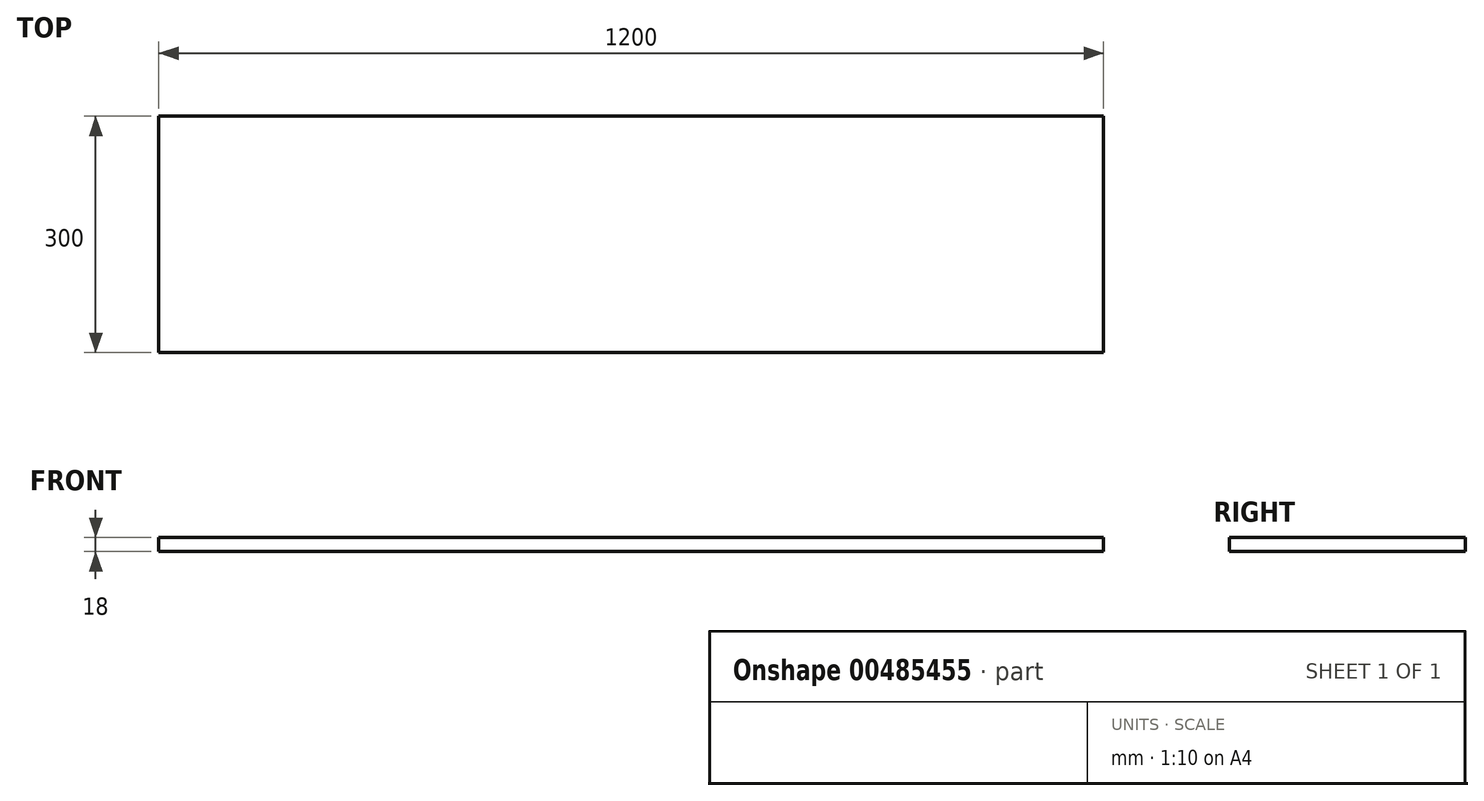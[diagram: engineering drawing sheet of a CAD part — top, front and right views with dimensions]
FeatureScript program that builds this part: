
annotation { "Feature Type Name" : "Feature", "Feature Type Description" : "" }
export const myFeature = defineFeature(function(context is Context, id is Id, definition is map)
    precondition{}
    {
        {
            var Q0;
            Q0=qCreatedBy(makeId("Top.planeOp"),FACE);
            var sketch = newSketch(context, id + "F0", { "sketchPlane" : qUnion([Q0])});
            skLineSegment(sketch, "E0.bottom", {"start": v(600, 150) * mm, "end": v(-600, 150) * mm});
            skLineSegment(sketch, "E0.top", {"start": v(600, -150) * mm, "end": v(-600, -150) * mm});
            skLineSegment(sketch, "E0.left", {"start": v(600, 150) * mm, "end": v(600, -150) * mm});
            skLineSegment(sketch, "E0.right", {"start": v(-600, 150) * mm, "end": v(-600, -150) * mm});
            skPoint(sketch, "E0.middle", {"position": v(0, 0) * mm});
            skSolve(sketch);
        }
        {
            var Q0;
            Q0 = qSketchRegion(id + "F0", true);
            extrude(context, id + "F1", {"entities" : qUnion([Q0]), "depth" : 18 * mm});
        }
    });
